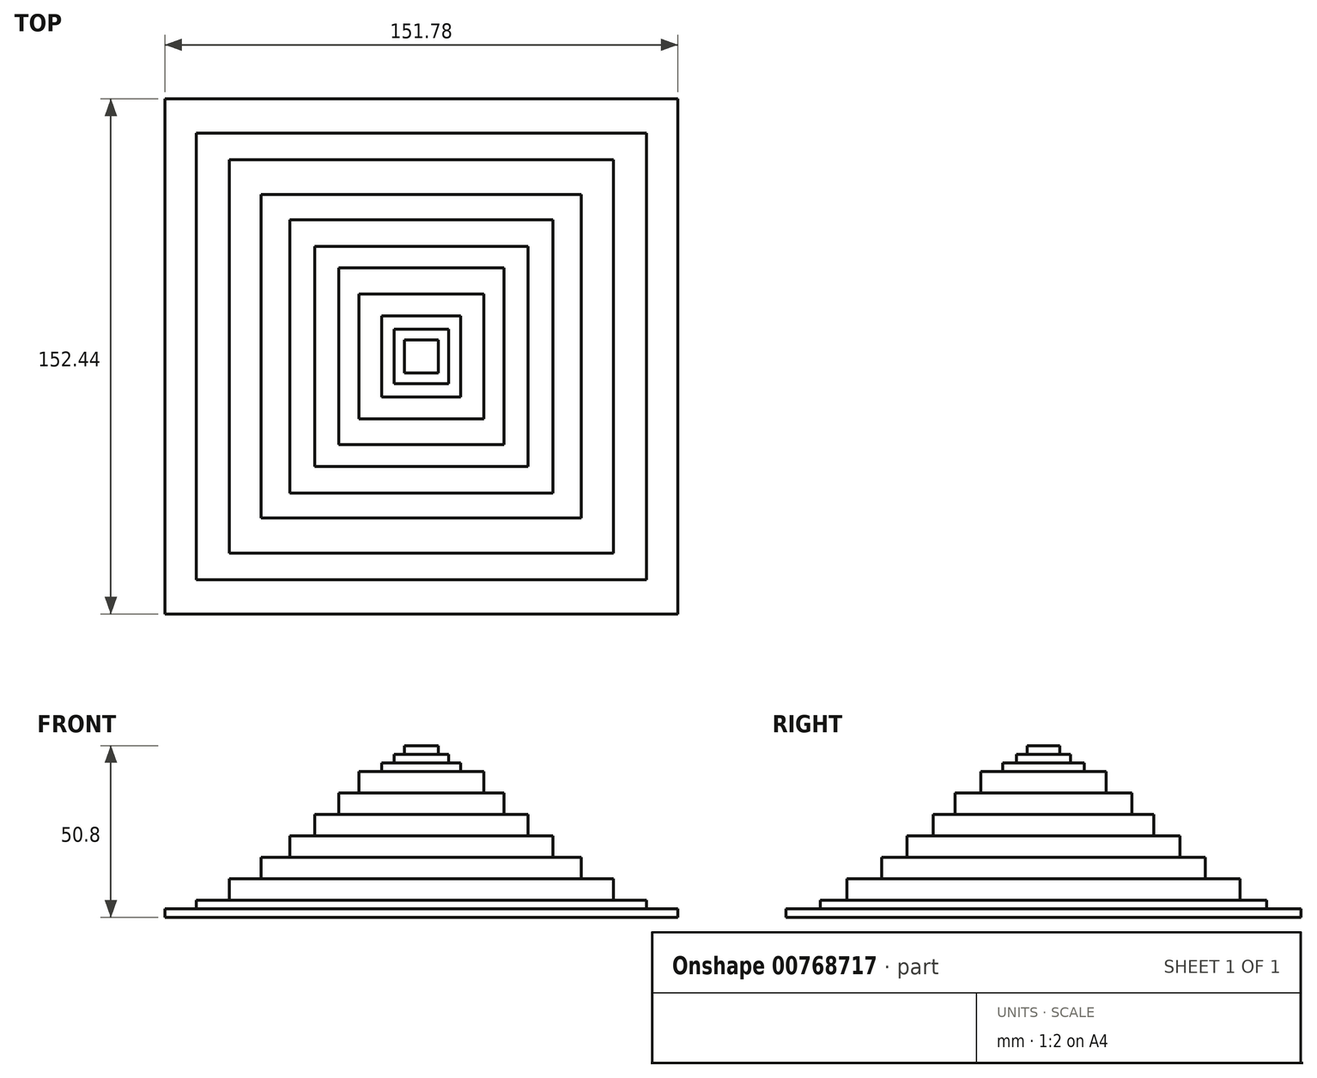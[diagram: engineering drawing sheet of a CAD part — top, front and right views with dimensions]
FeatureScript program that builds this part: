
annotation { "Feature Type Name" : "Feature", "Feature Type Description" : "" }
export const myFeature = defineFeature(function(context is Context, id is Id, definition is map)
    precondition{}
    {
        {
            var Q0;
            Q0=qCreatedBy(makeId("Top.planeOp"),FACE);
            var sketch = newSketch(context, id + "F0", { "sketchPlane" : qUnion([Q0])});
            skLineSegment(sketch, "E0.bottom", {"start": v(75.89, -76.22) * mm, "end": v(-75.89, -76.22) * mm});
            skLineSegment(sketch, "E0.top", {"start": v(75.89, 76.22) * mm, "end": v(-75.89, 76.22) * mm});
            skLineSegment(sketch, "E0.left", {"start": v(75.89, -76.22) * mm, "end": v(75.89, 76.22) * mm});
            skLineSegment(sketch, "E0.right", {"start": v(-75.89, -76.22) * mm, "end": v(-75.89, 76.22) * mm});
            skPoint(sketch, "E0.middle", {"position": v(0, 0) * mm});
            skSolve(sketch);
        }
        {
            var Q0;
            Q0 = qSketchRegion(id + "F0", true);
            extrude(context, id + "F1", {"entities" : qUnion([Q0]), "depth" : 2.54 * mm, "offsetDistance" : 25.4 * mm});
        }
        {
            var Q0;
            Q0=makeQuery(id+"F1.opExtrude","CAP_FACE",FACE,{"disambiguationData":[OSD([sQuery(id+"F0.wireOp",EDGE,"E0.bottom"),sQuery(id+"F0.wireOp",EDGE,"E0.top"),sQuery(id+"F0.wireOp",EDGE,"E0.left"),sQuery(id+"F0.wireOp",EDGE,"E0.right")])],"isStart":false});
            var sketch = newSketch(context, id + "F2", { "sketchPlane" : qUnion([Q0])});
            skLineSegment(sketch, "E1.bottom", {"start": v(66.6, -66.1) * mm, "end": v(-66.6, -66.1) * mm});
            skLineSegment(sketch, "E1.top", {"start": v(66.6, 66.1) * mm, "end": v(-66.6, 66.1) * mm});
            skLineSegment(sketch, "E1.left", {"start": v(66.6, -66.1) * mm, "end": v(66.6, 66.1) * mm});
            skLineSegment(sketch, "E1.right", {"start": v(-66.6, -66.1) * mm, "end": v(-66.6, 66.1) * mm});
            skPoint(sketch, "E1.middle", {"position": v(0, 0) * mm});
            skSolve(sketch);
        }
        {
            var Q0;
            Q0 = qSketchRegion(id + "F2", true);
            extrude(context, id + "F3", {"entities" : qUnion([Q0]), "operationType" : NewBodyOperationType.ADD, "depth" : 2.54 * mm, "offsetDistance" : 25.4 * mm});
        }
        {
            var Q0;
            Q0=makeQuery(id+"F3.opExtrude","CAP_FACE",FACE,{"disambiguationData":[OSD([sQuery(id+"F2.wireOp",EDGE,"E1.bottom"),sQuery(id+"F2.wireOp",EDGE,"E1.top"),sQuery(id+"F2.wireOp",EDGE,"E1.left"),sQuery(id+"F2.wireOp",EDGE,"E1.right")])],"isStart":false});
            var sketch = newSketch(context, id + "F4", { "sketchPlane" : qUnion([Q0])});
            skLineSegment(sketch, "E2.bottom", {"start": v(56.85, -58.21) * mm, "end": v(-56.85, -58.21) * mm});
            skLineSegment(sketch, "E2.top", {"start": v(56.85, 58.21) * mm, "end": v(-56.85, 58.21) * mm});
            skLineSegment(sketch, "E2.left", {"start": v(56.85, -58.21) * mm, "end": v(56.85, 58.21) * mm});
            skLineSegment(sketch, "E2.right", {"start": v(-56.85, -58.21) * mm, "end": v(-56.85, 58.21) * mm});
            skPoint(sketch, "E2.middle", {"position": v(0, 0) * mm});
            skSolve(sketch);
        }
        {
            var Q0;
            Q0 = qSketchRegion(id + "F4", true);
            extrude(context, id + "F5", {"entities" : qUnion([Q0]), "operationType" : NewBodyOperationType.ADD, "depth" : 6.35 * mm, "offsetDistance" : 25.4 * mm});
        }
        {
            var Q0;
            Q0=makeQuery(id+"F5.opExtrude","CAP_FACE",FACE,{"disambiguationData":[OSD([sQuery(id+"F4.wireOp",EDGE,"E2.bottom"),sQuery(id+"F4.wireOp",EDGE,"E2.top"),sQuery(id+"F4.wireOp",EDGE,"E2.left"),sQuery(id+"F4.wireOp",EDGE,"E2.right")])],"isStart":false});
            var sketch = newSketch(context, id + "F6", { "sketchPlane" : qUnion([Q0])});
            skLineSegment(sketch, "E3.bottom", {"start": v(47.35, -47.88) * mm, "end": v(-47.35, -47.88) * mm});
            skLineSegment(sketch, "E3.top", {"start": v(47.35, 47.88) * mm, "end": v(-47.35, 47.88) * mm});
            skLineSegment(sketch, "E3.left", {"start": v(47.35, -47.88) * mm, "end": v(47.35, 47.88) * mm});
            skLineSegment(sketch, "E3.right", {"start": v(-47.35, -47.88) * mm, "end": v(-47.35, 47.88) * mm});
            skPoint(sketch, "E3.middle", {"position": v(0, 0) * mm});
            skSolve(sketch);
        }
        {
            var Q0;
            Q0 = qSketchRegion(id + "F6", true);
            extrude(context, id + "F7", {"entities" : qUnion([Q0]), "operationType" : NewBodyOperationType.ADD, "depth" : 6.35 * mm, "offsetDistance" : 25.4 * mm});
        }
        {
            var Q0;
            Q0=makeQuery(id+"F7.opExtrude","CAP_FACE",FACE,{"disambiguationData":[OSD([sQuery(id+"F6.wireOp",EDGE,"E3.bottom"),sQuery(id+"F6.wireOp",EDGE,"E3.top"),sQuery(id+"F6.wireOp",EDGE,"E3.left"),sQuery(id+"F6.wireOp",EDGE,"E3.right")])],"isStart":false});
            var sketch = newSketch(context, id + "F8", { "sketchPlane" : qUnion([Q0])});
            skLineSegment(sketch, "E4.bottom", {"start": v(38.9, -40.43) * mm, "end": v(-38.9, -40.43) * mm});
            skLineSegment(sketch, "E4.top", {"start": v(38.9, 40.43) * mm, "end": v(-38.9, 40.43) * mm});
            skLineSegment(sketch, "E4.left", {"start": v(38.9, -40.43) * mm, "end": v(38.9, 40.43) * mm});
            skLineSegment(sketch, "E4.right", {"start": v(-38.9, -40.43) * mm, "end": v(-38.9, 40.43) * mm});
            skPoint(sketch, "E4.middle", {"position": v(0, 0) * mm});
            skSolve(sketch);
        }
        {
            var Q0;
            Q0 = qSketchRegion(id + "F8", true);
            extrude(context, id + "F9", {"entities" : qUnion([Q0]), "operationType" : NewBodyOperationType.ADD, "depth" : 6.35 * mm, "offsetDistance" : 25.4 * mm});
        }
        {
            var Q0;
            Q0=makeQuery(id+"F9.opExtrude","CAP_FACE",FACE,{"disambiguationData":[OSD([sQuery(id+"F8.wireOp",EDGE,"E4.bottom"),sQuery(id+"F8.wireOp",EDGE,"E4.top"),sQuery(id+"F8.wireOp",EDGE,"E4.left"),sQuery(id+"F8.wireOp",EDGE,"E4.right")])],"isStart":false});
            var sketch = newSketch(context, id + "F10", { "sketchPlane" : qUnion([Q0])});
            skLineSegment(sketch, "E5.bottom", {"start": v(31.56, -32.58) * mm, "end": v(-31.56, -32.58) * mm});
            skLineSegment(sketch, "E5.top", {"start": v(31.56, 32.58) * mm, "end": v(-31.56, 32.58) * mm});
            skLineSegment(sketch, "E5.left", {"start": v(31.56, -32.58) * mm, "end": v(31.56, 32.58) * mm});
            skLineSegment(sketch, "E5.right", {"start": v(-31.56, -32.58) * mm, "end": v(-31.56, 32.58) * mm});
            skPoint(sketch, "E5.middle", {"position": v(0, 0) * mm});
            skSolve(sketch);
        }
        {
            var Q0;
            Q0 = qSketchRegion(id + "F10", true);
            extrude(context, id + "F11", {"entities" : qUnion([Q0]), "operationType" : NewBodyOperationType.ADD, "depth" : 6.35 * mm, "offsetDistance" : 25.4 * mm});
        }
        {
            var Q0;
            Q0=makeQuery(id+"F11.opExtrude","CAP_FACE",FACE,{"disambiguationData":[OSD([sQuery(id+"F10.wireOp",EDGE,"E5.bottom"),sQuery(id+"F10.wireOp",EDGE,"E5.top"),sQuery(id+"F10.wireOp",EDGE,"E5.left"),sQuery(id+"F10.wireOp",EDGE,"E5.right")])],"isStart":false});
            var sketch = newSketch(context, id + "F12", { "sketchPlane" : qUnion([Q0])});
            skLineSegment(sketch, "E6.bottom", {"start": v(24.43, -26.15) * mm, "end": v(-24.43, -26.15) * mm});
            skLineSegment(sketch, "E6.top", {"start": v(24.43, 26.15) * mm, "end": v(-24.43, 26.15) * mm});
            skLineSegment(sketch, "E6.left", {"start": v(24.43, -26.15) * mm, "end": v(24.43, 26.15) * mm});
            skLineSegment(sketch, "E6.right", {"start": v(-24.43, -26.15) * mm, "end": v(-24.43, 26.15) * mm});
            skPoint(sketch, "E6.middle", {"position": v(0, 0) * mm});
            skSolve(sketch);
        }
        {
            var Q0;
            Q0 = qSketchRegion(id + "F12", true);
            extrude(context, id + "F13", {"entities" : qUnion([Q0]), "operationType" : NewBodyOperationType.ADD, "depth" : 6.35 * mm, "offsetDistance" : 25.4 * mm});
        }
        {
            var Q0;
            Q0=makeQuery(id+"F13.opExtrude","CAP_FACE",FACE,{"disambiguationData":[OSD([sQuery(id+"F12.wireOp",EDGE,"E6.bottom"),sQuery(id+"F12.wireOp",EDGE,"E6.top"),sQuery(id+"F12.wireOp",EDGE,"E6.left"),sQuery(id+"F12.wireOp",EDGE,"E6.right")])],"isStart":false});
            var sketch = newSketch(context, id + "F14", { "sketchPlane" : qUnion([Q0])});
            skLineSegment(sketch, "E7.bottom", {"start": v(18.5, -18.5) * mm, "end": v(-18.5, -18.5) * mm});
            skLineSegment(sketch, "E7.top", {"start": v(18.5, 18.5) * mm, "end": v(-18.5, 18.5) * mm});
            skLineSegment(sketch, "E7.left", {"start": v(18.5, -18.5) * mm, "end": v(18.5, 18.5) * mm});
            skLineSegment(sketch, "E7.right", {"start": v(-18.5, -18.5) * mm, "end": v(-18.5, 18.5) * mm});
            skPoint(sketch, "E7.middle", {"position": v(0, 0) * mm});
            skSolve(sketch);
        }
        {
            var Q0;
            Q0 = qSketchRegion(id + "F14", true);
            extrude(context, id + "F15", {"entities" : qUnion([Q0]), "operationType" : NewBodyOperationType.ADD, "depth" : 6.35 * mm, "offsetDistance" : 25.4 * mm});
        }
        {
            var Q0;
            Q0=makeQuery(id+"F15.opExtrude","CAP_FACE",FACE,{"disambiguationData":[OSD([sQuery(id+"F14.wireOp",EDGE,"E7.bottom"),sQuery(id+"F14.wireOp",EDGE,"E7.top"),sQuery(id+"F14.wireOp",EDGE,"E7.left"),sQuery(id+"F14.wireOp",EDGE,"E7.right")])],"isStart":false});
            var sketch = newSketch(context, id + "F16", { "sketchPlane" : qUnion([Q0])});
            skLineSegment(sketch, "E8.bottom", {"start": v(11.66, -12) * mm, "end": v(-11.66, -12) * mm});
            skLineSegment(sketch, "E8.top", {"start": v(11.66, 12) * mm, "end": v(-11.66, 12) * mm});
            skLineSegment(sketch, "E8.left", {"start": v(11.66, -12) * mm, "end": v(11.66, 12) * mm});
            skLineSegment(sketch, "E8.right", {"start": v(-11.66, -12) * mm, "end": v(-11.66, 12) * mm});
            skPoint(sketch, "E8.middle", {"position": v(0, 0) * mm});
            skSolve(sketch);
        }
        {
            var Q0;
            Q0 = qSketchRegion(id + "F16", true);
            extrude(context, id + "F17", {"entities" : qUnion([Q0]), "operationType" : NewBodyOperationType.ADD, "depth" : 2.54 * mm, "offsetDistance" : 25.4 * mm});
        }
        {
            var Q0;
            Q0=makeQuery(id+"F17.opExtrude","CAP_FACE",FACE,{"disambiguationData":[OSD([sQuery(id+"F16.wireOp",EDGE,"E8.bottom"),sQuery(id+"F16.wireOp",EDGE,"E8.top"),sQuery(id+"F16.wireOp",EDGE,"E8.left"),sQuery(id+"F16.wireOp",EDGE,"E8.right")])],"isStart":false});
            var sketch = newSketch(context, id + "F18", { "sketchPlane" : qUnion([Q0])});
            skLineSegment(sketch, "E9.bottom", {"start": v(8.03, -8.07) * mm, "end": v(-8.03, -8.07) * mm});
            skLineSegment(sketch, "E9.top", {"start": v(8.03, 8.07) * mm, "end": v(-8.03, 8.07) * mm});
            skLineSegment(sketch, "E9.left", {"start": v(8.03, -8.07) * mm, "end": v(8.03, 8.07) * mm});
            skLineSegment(sketch, "E9.right", {"start": v(-8.03, -8.07) * mm, "end": v(-8.03, 8.07) * mm});
            skPoint(sketch, "E9.middle", {"position": v(0, 0) * mm});
            skSolve(sketch);
        }
        {
            var Q0;
            Q0 = qSketchRegion(id + "F18", true);
            extrude(context, id + "F19", {"entities" : qUnion([Q0]), "operationType" : NewBodyOperationType.ADD, "depth" : 2.54 * mm, "offsetDistance" : 25.4 * mm});
        }
        {
            var Q0;
            Q0=makeQuery(id+"F19.opExtrude","CAP_FACE",FACE,{"disambiguationData":[OSD([sQuery(id+"F18.wireOp",EDGE,"E9.bottom"),sQuery(id+"F18.wireOp",EDGE,"E9.top"),sQuery(id+"F18.wireOp",EDGE,"E9.left"),sQuery(id+"F18.wireOp",EDGE,"E9.right")])],"isStart":false});
            var sketch = newSketch(context, id + "F20", { "sketchPlane" : qUnion([Q0])});
            skLineSegment(sketch, "E10.bottom", {"start": v(5, -4.87) * mm, "end": v(-5, -4.87) * mm});
            skLineSegment(sketch, "E10.top", {"start": v(5, 4.87) * mm, "end": v(-5, 4.87) * mm});
            skLineSegment(sketch, "E10.left", {"start": v(5, -4.87) * mm, "end": v(5, 4.87) * mm});
            skLineSegment(sketch, "E10.right", {"start": v(-5, -4.87) * mm, "end": v(-5, 4.87) * mm});
            skPoint(sketch, "E10.middle", {"position": v(0, 0) * mm});
            skSolve(sketch);
        }
        {
            var Q0;
            Q0=makeQuery(id+"F20.imprint","IMPRINT",FACE,{"disambiguationData":[TD([[makeQuery(id+"F20.imprint","IMPRINT",EDGE,{"derivedFrom":sQuery(id+"F20.wireOp",EDGE,"E10.bottom")}),-1.0]])]});
            var Q1;
            Q1 = qSketchRegion(id + "F20", true);
            extrude(context, id + "F21", {"entities" : qUnion([Q0, Q1]), "operationType" : NewBodyOperationType.ADD, "depth" : 2.54 * mm, "offsetDistance" : 25.4 * mm});
        }
    });
